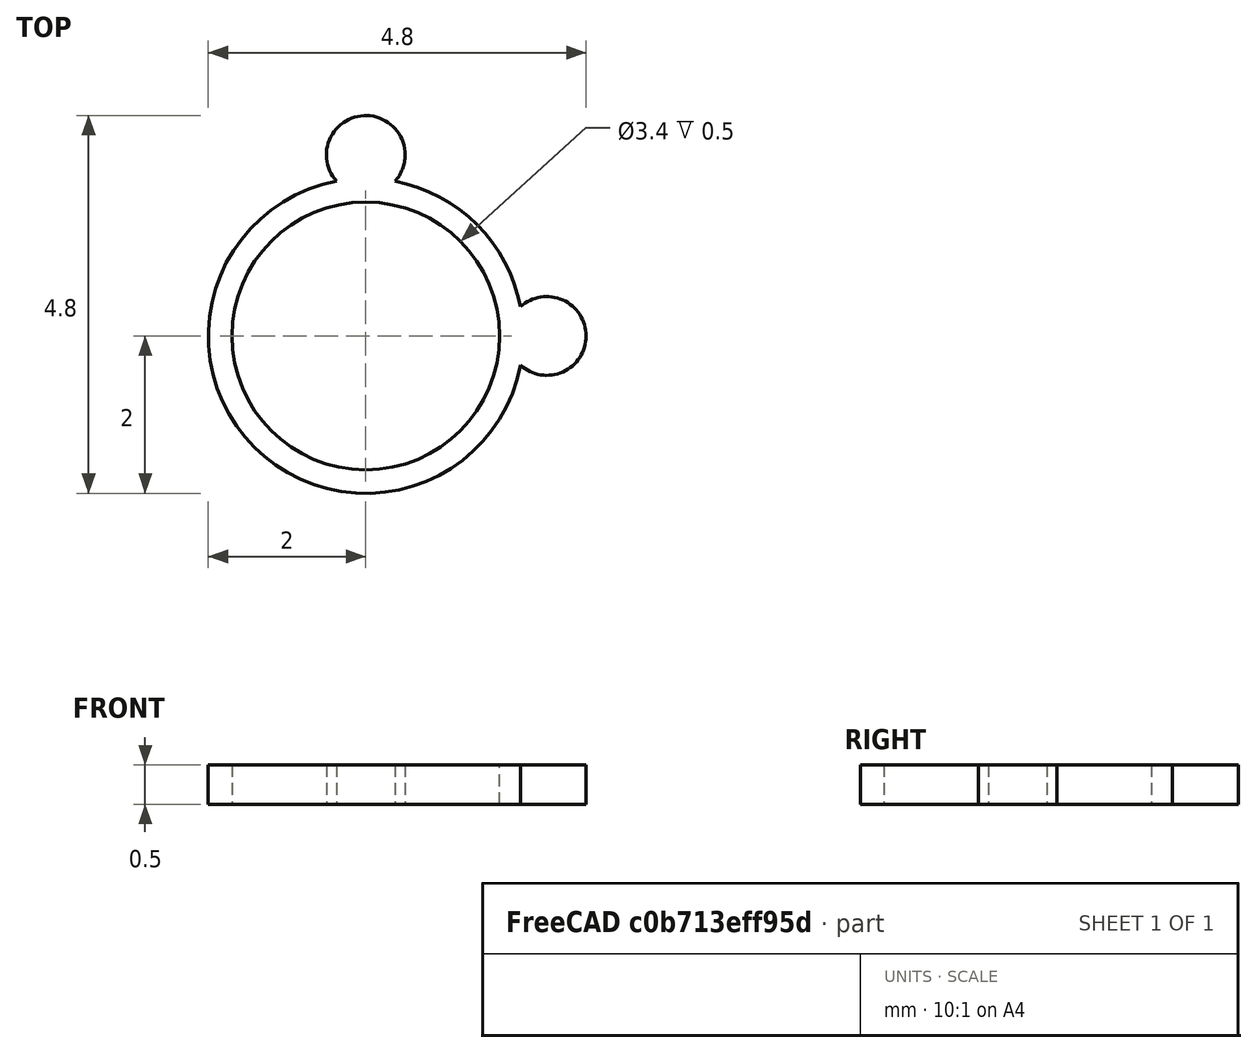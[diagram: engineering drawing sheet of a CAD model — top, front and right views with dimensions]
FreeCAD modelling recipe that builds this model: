
FCSTD DOCUMENT  (FreeCAD 0.20R29177 +233 (Git))
Label: anillo-osito
License: Creative Commons Attribution-ShareAlike
LicenseURL: http://creativecommons.org/licenses/by-sa/4.0/
objects: Part::Cylinder×4, Part::MultiFuse×2, Part::Cut×1
note: 7 computed .brp shape members not serialized (recipe doc carries the construction recipe); baked Part::Feature solids carry a one-line shape summary decoded from their .brp

FEATURE [Part::Cylinder] Cylinder  label="Cilindro"
  Angle = 360
  AttacherType = Attacher::AttachEngine3D
  FirstAngle = 0
  Height = 0.5
  Radius = 2
  SecondAngle = 0
FEATURE [Part::Cylinder] Cylinder001  label="Cilindro001"
  Angle = 360
  AttacherType = Attacher::AttachEngine3D
  FirstAngle = 0
  Height = 0.5
  Radius = 1.7
  SecondAngle = 0
FEATURE [Part::Cut] Cut
  Base = -> Cylinder
  Refine = true
  Tool = -> Cylinder001
FEATURE [Part::Cylinder] Cylinder002  label="Cilindro002"
  Angle = 360
  AttacherType = Attacher::AttachEngine3D
  FirstAngle = 0
  Height = 0.5
  Placement = pos=(2.3,0,0) rot=(0,0,1;0rad)
  Radius = 0.5
  SecondAngle = 0
FEATURE [Part::Cylinder] Cylinder003  label="Cilindro003"
  Angle = 360
  AttacherType = Attacher::AttachEngine3D
  FirstAngle = 0
  Height = 0.5
  Placement = pos=(0,2.3,0) rot=(0,0,1;0rad)
  Radius = 0.5
  SecondAngle = 0
FEATURE [Part::MultiFuse] Fusion
  Refine = true
  Shapes = -> [Cut,Cylinder002]
FEATURE [Part::MultiFuse] Fusion001
  Refine = true
  Shapes = -> [Fusion,Cylinder003]
